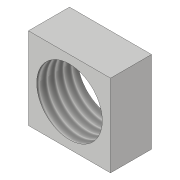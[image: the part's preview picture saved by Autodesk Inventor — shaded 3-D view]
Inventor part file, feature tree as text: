
AUTODESK INVENTOR PART (.ipt)
format: ipt  version: 2019 (Build 230136000, 136)  size: 93,696 bytes
history: native  units: in
note: dims shown in document units (in); Inventor stores cm internally (conversion verified against a paired STEP export)
features: extrude x2, sketch x2, thread x1
ambient origin geometry x8: Origin, YZ Plane, XZ Plane, XY Plane, X Axis, Y Axis, Z Axis, Center Point
bodies: Solid1 (feature_tree)
feature tree (5):
  extrude  "Extrusion1"  Depth=0.7874in
  extrude  "Extrusion2"  Depth=0.3937in
  thread  "Thread1"  [1 undecoded]
  sketch  "Sketch1"  dims[d0=0.7874in d1=0.7874in]
  sketch  "Sketch2"  dims[d2=0.3937in d3=0.0in d4=0.3937in d5=0.3937in d6=0.6299in d7=0.0in d8=0.0in d9=0.3937in d10=0.0in]
note: 1 required parameter value undecoded (feature->parameter linkage not recoverable at this tier; creation-order binding heuristic only, values carry confidence <= 0.55)
